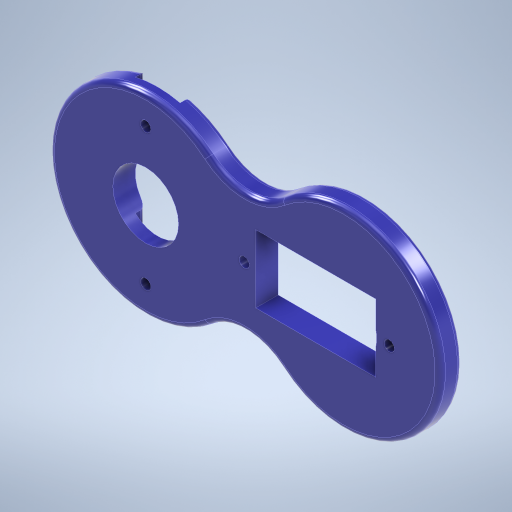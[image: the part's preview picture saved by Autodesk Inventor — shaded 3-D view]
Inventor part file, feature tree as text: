
AUTODESK INVENTOR PART (.ipt)
format: ipt  version: 2023.2 (Build 272271000, 271)  size: 360,960 bytes
history: native  units: mm
features: sketch x5, extrude x3, hole x2, fillet x1
ambient origin geometry x8: Origin, YZ Plane, XZ Plane, XY Plane, X Axis, Y Axis, Z Axis, Center Point
bodies: Solid1 (feature_tree)
feature tree (11):
  extrude  "Extrusion1"  Depth=4.3mm TaperAngle=0.0deg
  hole  "Hole1"  [1 undecoded]
  extrude  "Extrusion2"  Depth=2.0mm
  extrude  "Extrusion3"  Depth=2.0mm
  fillet  "Fillet1"  Radius=23.0mm
  hole  "Hole2"  [1 undecoded]
  sketch  "Sketch2"  dims[d0=37.0mm d5=4.3mm d6=0.0mm]
  sketch  "Sketch3"  dims[d7=27.8mm]
  sketch  "Sketch4"  dims[d8=2.0mm d9=6.0mm d10=4.0mm d11=2.0mm d12=90.0deg d13=7.0mm d14=0.0mm d16=8.7mm]
  sketch  "Sketch5"  dims[d17=2.0mm d18=0.0mm d19=12.6mm]
  sketch  "Sketch7"  dims[d20=37.0mm d21=13.0mm d22=23.0mm d23=2.6mm d24=4.3mm d25=0.0mm d26=38.0mm d27=1.0mm d28=26.2mm d29=2.0mm d30=6.0mm d31=4.0mm d32=2.0mm d33=90.0deg d34=7.0mm d35=0.0mm]
note: 2 required parameter values undecoded (feature->parameter linkage not recoverable at this tier; creation-order binding heuristic only, values carry confidence <= 0.55)
